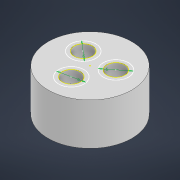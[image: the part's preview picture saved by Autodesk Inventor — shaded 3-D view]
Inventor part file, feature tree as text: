
AUTODESK INVENTOR PART (.ipt)
format: ipt  version: 2021 (Build 250183000, 183)  size: 116,224 bytes
history: native  units: mm
features: sketch x3, projected_geometry x3, extrude x2
ambient origin geometry x8: Origin, YZ Plane, XZ Plane, XY Plane, X Axis, Y Axis, Z Axis, Center Point
bodies: Volumenkörper1 (feature_tree)
feature tree (8):
  extrude  "Extrusion1"  Depth=10.0mm TaperAngle=0.0deg
  extrude  "Extrusion3"  Depth=4.5mm
  sketch  "Skizze3"  dims[d19=4.5mm d20=120.0deg d21=120.0deg d22=4.3mm d23=4.3mm d24=4.3mm d25=6.0mm d26=0.0mm d27=6.0mm d28=6.0mm d29=6.0mm]
  sketch  "Skizze1"  dims[d0=20.0mm d1=10.0mm d2=0.0mm]
  sketch  "Skizze2"  dims[d17=4.5mm d18=4.5mm]
  projected_geometry  "Projizierte Kontur1"
  projected_geometry  "Projizierte Kontur2"
  projected_geometry  "Projizierte Kontur3"
